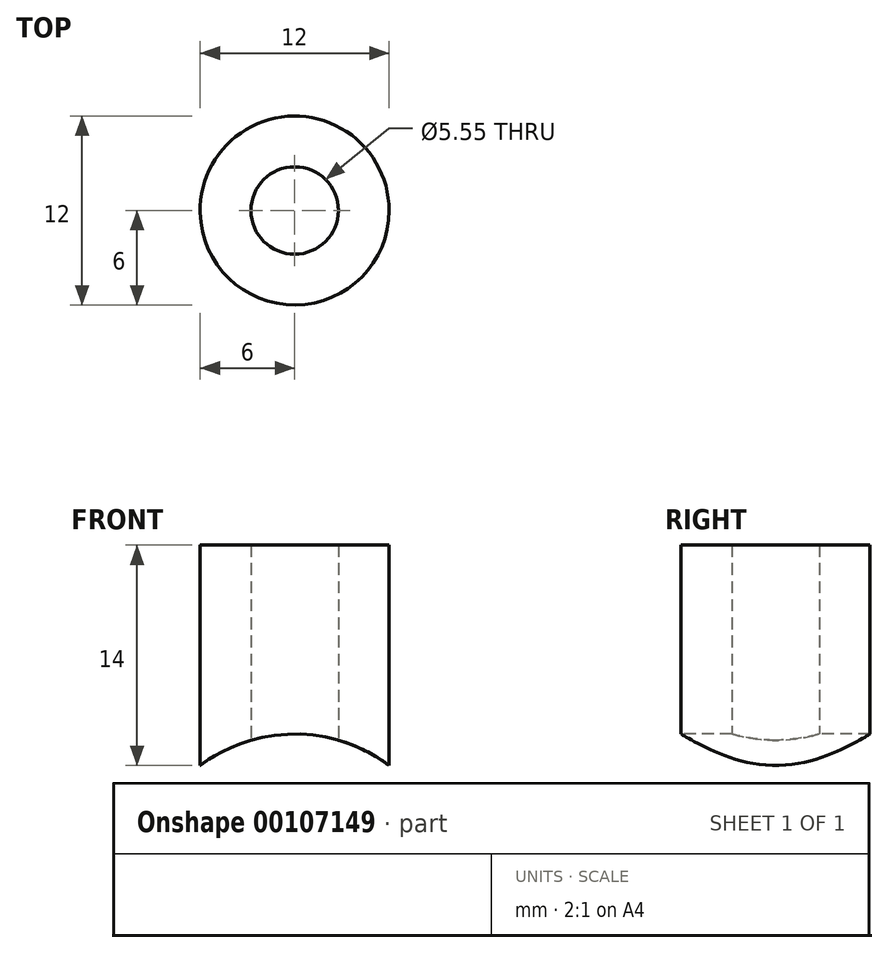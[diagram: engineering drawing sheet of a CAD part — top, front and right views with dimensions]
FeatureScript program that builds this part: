
annotation { "Feature Type Name" : "Feature", "Feature Type Description" : "" }
export const myFeature = defineFeature(function(context is Context, id is Id, definition is map)
    precondition{}
    {
        {
            var Q0;
            Q0=qCreatedBy(makeId("Top.planeOp"),FACE);
            var sketch = newSketch(context, id + "F0", { "sketchPlane" : qUnion([Q0])});
            skCircle(sketch, "E0", {"center": v(0, 0) * mm, "radius": 2.77 * mm});
            skCircle(sketch, "E1", {"center": v(0, 0) * mm, "radius": 6 * mm});
            skSolve(sketch);
        }
        {
            var Q0;
            Q0 = qSketchRegion(id + "F0", true);
            extrude(context, id + "F1", {"entities" : qUnion([Q0]), "depth" : 14 * mm});
        }
        {
            var Q0;
            Q0=qCreatedBy(makeId("Front.planeOp"),FACE);
            var sketch = newSketch(context, id + "F2", { "sketchPlane" : qUnion([Q0])});
            skLineSegment(sketch, "E2", {"start": v(-9.92, 0) * mm, "end": v(-6, 0) * mm, "construction": true});
            skLineSegment(sketch, "E3", {"start": v(6, 1.49) * mm, "end": v(6, -4.59) * mm, "construction": true});
            skLineSegment(sketch, "E4", {"start": v(-6, 3.36) * mm, "end": v(-6, -3.35) * mm, "construction": true});
            skArc(sketch, "E5", {"start": v(6, 0) * mm, "mid": v(0, 2) * mm, "end": v(-6, 0) * mm});
            skLineSegment(sketch, "E6", {"start": v(0, 2) * mm, "end": v(10.48, 2) * mm, "construction": true});
            skLineSegment(sketch, "E7", {"start": v(-2.74, 14) * mm, "end": v(7.22, 14) * mm, "construction": true});
            skLineSegment(sketch, "E8", {"start": v(-6, 0) * mm, "end": v(6, 0) * mm});
            skLineSegment(sketch, "E9.trimOffspring", {"start": v(6, 0) * mm, "end": v(9.08, 0) * mm, "construction": true});
            skLineSegment(sketch, "E10", {"start": v(-6, 0) * mm, "end": v(-6, -0.05) * mm});
            skLineSegment(sketch, "E11", {"start": v(-6, -0.05) * mm, "end": v(-6, -0.8) * mm});
            skLineSegment(sketch, "E12", {"start": v(-6, -0.8) * mm, "end": v(6, -0.8) * mm});
            skLineSegment(sketch, "E13", {"start": v(6, -0.8) * mm, "end": v(6, 0) * mm});
            skSolve(sketch);
        }
        {
            var Q0;
            Q0 = qSketchRegion(id + "F2", true);
            extrude(context, id + "F3", {"entities" : qUnion([Q0]), "operationType" : NewBodyOperationType.REMOVE, "endBound" : BoundingType.SYMMETRIC, "oppositeDirection" : true, "depth" : 25 * mm});
        }
    });
